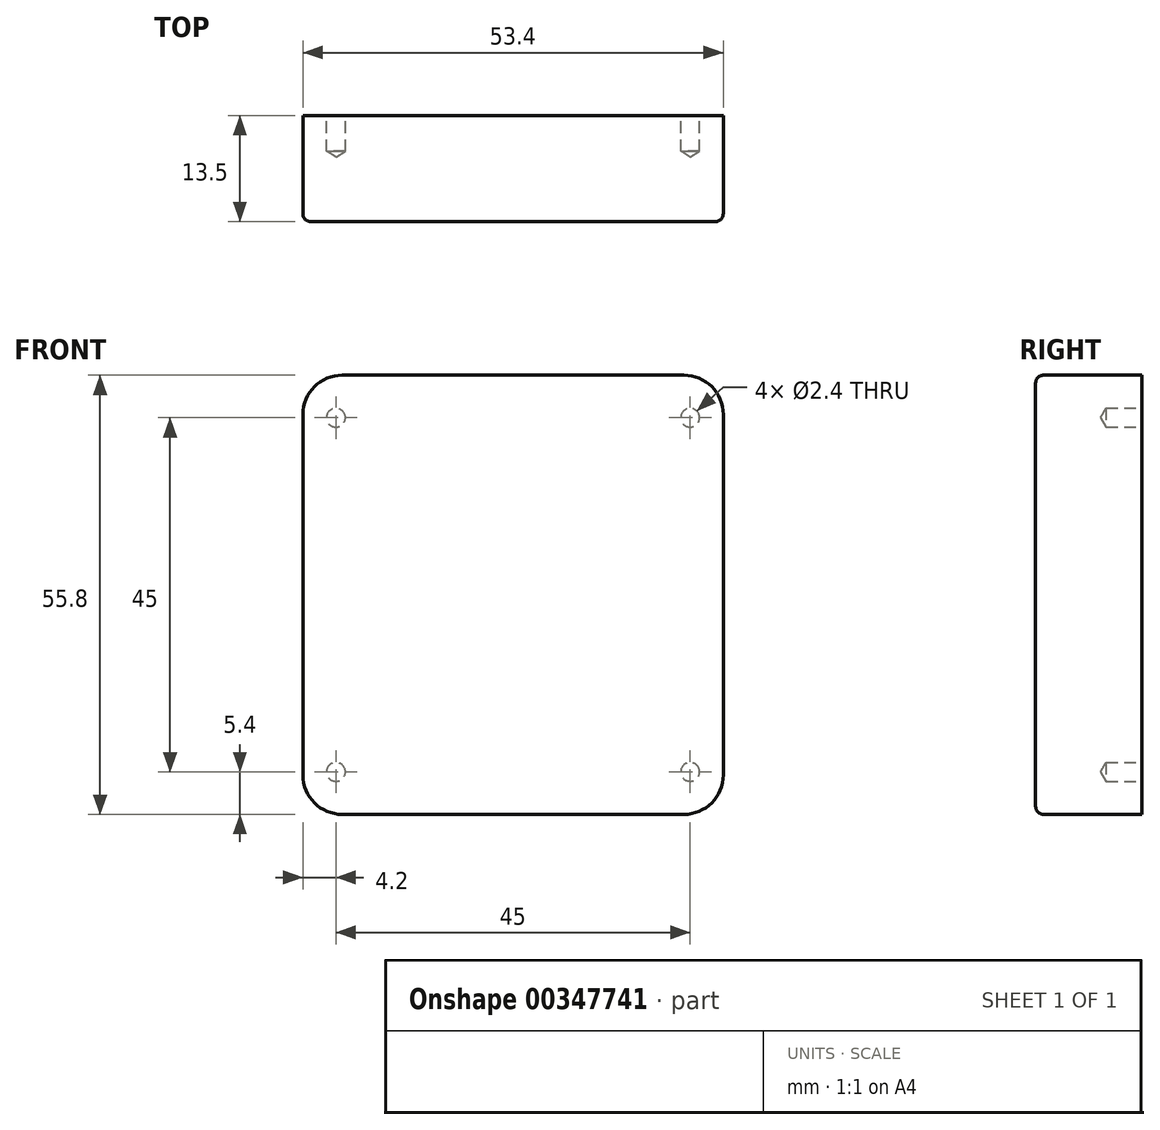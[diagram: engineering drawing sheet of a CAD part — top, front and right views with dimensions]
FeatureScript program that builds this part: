
annotation { "Feature Type Name" : "Feature", "Feature Type Description" : "" }
export const myFeature = defineFeature(function(context is Context, id is Id, definition is map)
    precondition{}
    {
        {
            var Q0;
            Q0=qCreatedBy(makeId("Front.planeOp"),FACE);
            var sketch = newSketch(context, id + "F0", { "sketchPlane" : qUnion([Q0])});
            skLineSegment(sketch, "E0.bottom", {"start": v(-26.7, 27.9) * mm, "end": v(26.7, 27.9) * mm});
            skLineSegment(sketch, "E0.top", {"start": v(-26.7, -27.9) * mm, "end": v(26.7, -27.9) * mm});
            skLineSegment(sketch, "E0.left", {"start": v(-26.7, 27.9) * mm, "end": v(-26.7, -27.9) * mm});
            skLineSegment(sketch, "E0.right", {"start": v(26.7, 27.9) * mm, "end": v(26.7, -27.9) * mm});
            skPoint(sketch, "E0.middle", {"position": v(0, 0) * mm});
            skSolve(sketch);
        }
        {
            var Q0;
            Q0 = qSketchRegion(id + "F0", true);
            extrude(context, id + "F1", {"entities" : qUnion([Q0]), "depth" : 13.5 * mm});
        }
        {
            var Q0;
            Q0=makeQuery(id+"F1.opExtrude","SWEPT_EDGE",EDGE,{"disambiguationData":[OSD([sQuery(id+"F0.wireOp",EDGE,"E0.bottom"),sQuery(id+"F0.wireOp",EDGE,"E0.left")])]});
            var Q1;
            Q1=makeQuery(id+"F1.opExtrude","SWEPT_EDGE",EDGE,{"disambiguationData":[OSD([sQuery(id+"F0.wireOp",EDGE,"E0.bottom"),sQuery(id+"F0.wireOp",EDGE,"E0.right")])]});
            var Q2;
            Q2=makeQuery(id+"F1.opExtrude","SWEPT_EDGE",EDGE,{"disambiguationData":[OSD([sQuery(id+"F0.wireOp",EDGE,"E0.top"),sQuery(id+"F0.wireOp",EDGE,"E0.right")])]});
            var Q3;
            Q3=makeQuery(id+"F1.opExtrude","SWEPT_EDGE",EDGE,{"disambiguationData":[OSD([sQuery(id+"F0.wireOp",EDGE,"E0.top"),sQuery(id+"F0.wireOp",EDGE,"E0.left")])]});
            fillet(context, id + "F2", {"entities" : qUnion([Q0, Q1, Q2, Q3]), "radius" : 5 * mm, "tangentPropagation" : true, "allowEdgeOverflow" : false});
        }
        {
            var Q0;
            Q0=makeQuery(id+"F1.opExtrude","CAP_EDGE",EDGE,{"disambiguationData":[OSD([sQuery(id+"F0.wireOp",EDGE,"E0.bottom")])],"isStart":false});
            fillet(context, id + "F3", {"entities" : qUnion([Q0]), "radius" : 1 * mm, "tangentPropagation" : true, "allowEdgeOverflow" : false});
        }
        {
            var Q0;
            Q0=makeQuery(id+"F1.opExtrude","CAP_FACE",FACE,{"disambiguationData":[OSD([sQuery(id+"F0.wireOp",EDGE,"E0.bottom"),sQuery(id+"F0.wireOp",EDGE,"E0.top"),sQuery(id+"F0.wireOp",EDGE,"E0.left"),sQuery(id+"F0.wireOp",EDGE,"E0.right")])],"isStart":true});
            var sketch = newSketch(context, id + "F4", { "sketchPlane" : qUnion([Q0])});
            skLineSegment(sketch, "E1.bottom", {"start": v(22.5, -22.5) * mm, "end": v(-22.5, -22.5) * mm, "construction": true});
            skLineSegment(sketch, "E1.top", {"start": v(22.5, 22.5) * mm, "end": v(-22.5, 22.5) * mm, "construction": true});
            skLineSegment(sketch, "E1.left", {"start": v(22.5, -22.5) * mm, "end": v(22.5, 22.5) * mm, "construction": true});
            skLineSegment(sketch, "E1.right", {"start": v(-22.5, -22.5) * mm, "end": v(-22.5, 22.5) * mm, "construction": true});
            skPoint(sketch, "E1.middle", {"position": v(0, 0) * mm});
            skCircle(sketch, "E2", {"center": v(-22.5, 22.5) * mm, "radius": 2.07 * mm});
            skCircle(sketch, "E3", {"center": v(22.5, 22.5) * mm, "radius": 2.17 * mm});
            skCircle(sketch, "E4", {"center": v(22.5, -22.5) * mm, "radius": 2.13 * mm});
            skCircle(sketch, "E5", {"center": v(-22.5, -22.5) * mm, "radius": 2.75 * mm});
            skSolve(sketch);
        }
        {
            var Q0;
            Q0=sQuery(id+"F4.wireOp",VERTEX,"E2.center");
            var Q1;
            Q1=sQuery(id+"F4.wireOp",VERTEX,"E3.center");
            var Q2;
            Q2=sQuery(id+"F4.wireOp",VERTEX,"E4.center");
            var Q3;
            Q3=sQuery(id+"F4.wireOp",VERTEX,"E5.center");
            var Q4;
            Q4=makeQuery(id+"F1.opExtrude","SWEPT_BODY",BODY,{"disambiguationData":[OSD([sQuery(id+"F0.wireOp",EDGE,"E0.bottom"),sQuery(id+"F0.wireOp",EDGE,"E0.top"),sQuery(id+"F0.wireOp",EDGE,"E0.left"),sQuery(id+"F0.wireOp",EDGE,"E0.right")])]});
            hole(context, id + "F5", {"style" : HoleStyle.SIMPLE, "endStyle" : HoleEndStyle.BLIND, "standardTappedOrClearance" : lookupTablePath({ "standard" : "ISO", "engagement" : "75%", "pitch" : "0.6 mm", "size" : "M3", "type" : "Tapped" }), "standardBlindInLast" : lookupTablePath({ "standard" : "ISO", "engagement" : "75%", "pitch" : "0.6 mm", "size" : "M3", "type" : "Tapped" }), "holeDiameter" : 2.4 * mm, "showTappedDepth" : true, "holeDepth" : 4.55 * mm, "isTappedThrough" : true, "tappedDepth" : 2.75 * mm, "tapClearance" : 3, "startFromSketch" : true, "locations" : qUnion([Q0, Q1, Q2, Q3]), "scope" : qUnion([Q4])});
        }
    });
